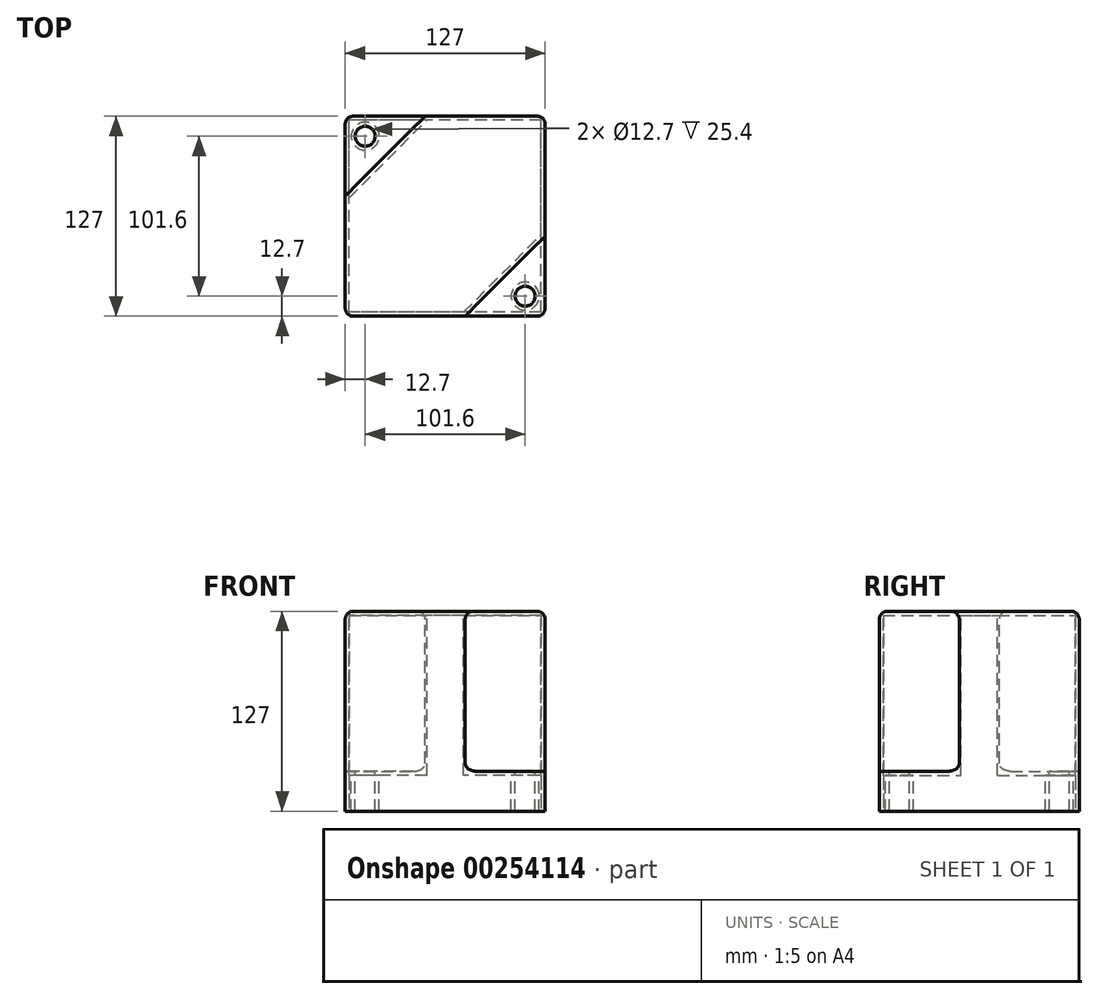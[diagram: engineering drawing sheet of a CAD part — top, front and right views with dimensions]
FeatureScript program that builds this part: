
annotation { "Feature Type Name" : "Feature", "Feature Type Description" : "" }
export const myFeature = defineFeature(function(context is Context, id is Id, definition is map)
    precondition{}
    {
        {
            var Q0;
            Q0=qCreatedBy(makeId("Top.planeOp"),FACE);
            var sketch = newSketch(context, id + "F0", { "sketchPlane" : qUnion([Q0])});
            skLineSegment(sketch, "E0.bottom", {"start": v(63.5, -63.5) * mm, "end": v(-63.5, -63.5) * mm});
            skLineSegment(sketch, "E0.top", {"start": v(63.5, 63.5) * mm, "end": v(-63.5, 63.5) * mm});
            skLineSegment(sketch, "E0.left", {"start": v(63.5, -63.5) * mm, "end": v(63.5, 63.5) * mm});
            skLineSegment(sketch, "E0.right", {"start": v(-63.5, -63.5) * mm, "end": v(-63.5, 63.5) * mm});
            skPoint(sketch, "E0.middle", {"position": v(0, 0) * mm});
            skSolve(sketch);
        }
        {
            var Q0;
            Q0=makeQuery(id+"F0.imprint","IMPRINT",FACE,{"disambiguationData":[TD([[makeQuery(id+"F0.imprint","IMPRINT",EDGE,{"derivedFrom":sQuery(id+"F0.wireOp",EDGE,"E0.bottom")}),-1.0]])]});
            extrude(context, id + "F1", {"entities" : qUnion([Q0]), "depth" : 127 * mm});
        }
        {
            var Q0;
            Q0=makeQuery(id+"F1.opExtrude","CAP_FACE",FACE,{"disambiguationData":[OSD([sQuery(id+"F0.wireOp",EDGE,"E0.bottom"),sQuery(id+"F0.wireOp",EDGE,"E0.top"),sQuery(id+"F0.wireOp",EDGE,"E0.left"),sQuery(id+"F0.wireOp",EDGE,"E0.right")])],"isStart":false});
            var sketch = newSketch(context, id + "F2", { "sketchPlane" : qUnion([Q0])});
            skLineSegment(sketch, "E1", {"start": v(-63.5, 63.5) * mm, "end": v(-63.5, 12.7) * mm});
            skLineSegment(sketch, "E2", {"start": v(-63.5, 63.5) * mm, "end": v(-12.7, 63.5) * mm});
            skLineSegment(sketch, "E3", {"start": v(63.5, -63.5) * mm, "end": v(12.7, -63.5) * mm});
            skLineSegment(sketch, "E4", {"start": v(63.5, -63.5) * mm, "end": v(63.5, -12.7) * mm});
            skLineSegment(sketch, "E5", {"start": v(-63.5, 12.7) * mm, "end": v(-12.7, 63.5) * mm});
            skLineSegment(sketch, "E6", {"start": v(12.7, -63.5) * mm, "end": v(63.5, -12.7) * mm});
            skSolve(sketch);
        }
        {
            var Q0;
            Q0 = qSketchRegion(id + "F2", true);
            extrude(context, id + "F3", {"entities" : qUnion([Q0]), "operationType" : NewBodyOperationType.REMOVE, "oppositeDirection" : true, "depth" : 101.6 * mm});
        }
        {
            var Q0;
            Q0=makeQuery(id+"F3.boolean.opBoolean","COPY",FACE,{"derivedFrom":makeQuery(id+"F3.opExtrude","CAP_FACE",FACE,{"disambiguationData":[OSD([sQuery(id+"F2.wireOp",EDGE,"E1"),sQuery(id+"F2.wireOp",EDGE,"E2"),sQuery(id+"F2.wireOp",EDGE,"E5")])],"isStart":false})});
            var sketch = newSketch(context, id + "F4", { "sketchPlane" : qUnion([Q0])});
            skCircle(sketch, "E7", {"center": v(-50.8, 50.8) * mm, "radius": 6.35 * mm});
            skCircle(sketch, "E8", {"center": v(50.8, -50.8) * mm, "radius": 6.35 * mm});
            skSolve(sketch);
        }
        {
            var Q0;
            Q0=makeQuery(id+"F4.imprint","IMPRINT",FACE,{"disambiguationData":[TD([[makeQuery(id+"F4.imprint","IMPRINT",EDGE,{"derivedFrom":sQuery(id+"F4.wireOp",EDGE,"E7")}),1.0]])]});
            var Q1;
            Q1=makeQuery(id+"F4.imprint","IMPRINT",FACE,{"disambiguationData":[TD([[makeQuery(id+"F4.imprint","IMPRINT",EDGE,{"derivedFrom":sQuery(id+"F4.wireOp",EDGE,"E8")}),1.0]])]});
            extrude(context, id + "F5", {"entities" : qUnion([Q0, Q1]), "operationType" : NewBodyOperationType.REMOVE, "oppositeDirection" : true, "depth" : 203.2 * mm});
        }
        {
            var Q0;
            Q0=makeQuery(id+"F1.opExtrude","CAP_FACE",FACE,{"disambiguationData":[OSD([sQuery(id+"F0.wireOp",EDGE,"E0.bottom"),sQuery(id+"F0.wireOp",EDGE,"E0.top"),sQuery(id+"F0.wireOp",EDGE,"E0.left"),sQuery(id+"F0.wireOp",EDGE,"E0.right")])],"isStart":true});
            shell(context, id + "F6", {"entities" : qUnion([Q0]), "thickness" : 2.54 * mm});
        }
        {
            var Q0;
            Q0=makeQuery(id+"F3.boolean.opBoolean","COPY",EDGE,{"derivedFrom":makeQuery(id+"F3.opExtrude","CAP_EDGE",EDGE,{"disambiguationData":[OSD([sQuery(id+"F2.wireOp",EDGE,"E6")])],"isStart":true})});
            var Q1;
            Q1=makeQuery(id+"F1.opExtrude","CAP_EDGE",EDGE,{"disambiguationData":[OSD([sQuery(id+"F0.wireOp",EDGE,"E0.bottom")])],"isStart":false});
            var Q2;
            Q2=makeQuery(id+"F3.boolean.opBoolean","COPY",EDGE,{"derivedFrom":makeQuery(id+"F3.opExtrude","SWEPT_EDGE",EDGE,{"disambiguationData":[OSD([sQuery(id+"F0.wireOp",EDGE,"E0.bottom"),sQuery(id+"F2.wireOp",EDGE,"E3"),sQuery(id+"F2.wireOp",EDGE,"E6")])]})});
            var Q3;
            Q3=makeQuery(id+"F3.boolean.opBoolean","COPY",EDGE,{"derivedFrom":makeQuery(id+"F3.opExtrude","SWEPT_EDGE",EDGE,{"disambiguationData":[OSD([sQuery(id+"F0.wireOp",EDGE,"E0.left"),sQuery(id+"F2.wireOp",EDGE,"E4"),sQuery(id+"F2.wireOp",EDGE,"E6")])]})});
            var Q4;
            Q4=makeQuery(id+"F1.opExtrude","CAP_EDGE",EDGE,{"disambiguationData":[OSD([sQuery(id+"F0.wireOp",EDGE,"E0.left")])],"isStart":false});
            var Q5;
            Q5=makeQuery(id+"F3.boolean.opBoolean","COPY",EDGE,{"derivedFrom":makeQuery(id+"F3.opExtrude","CAP_EDGE",EDGE,{"disambiguationData":[OSD([sQuery(id+"F2.wireOp",EDGE,"E4")])],"isStart":false})});
            var Q6;
            Q6=makeQuery(id+"F3.boolean.opBoolean","COPY",EDGE,{"derivedFrom":makeQuery(id+"F3.opExtrude","CAP_EDGE",EDGE,{"disambiguationData":[OSD([sQuery(id+"F2.wireOp",EDGE,"E3")])],"isStart":false})});
            var Q7;
            Q7=makeQuery(id+"F3.boolean.opBoolean","COPY",EDGE,{"derivedFrom":makeQuery(id+"F3.opExtrude","CAP_EDGE",EDGE,{"disambiguationData":[OSD([sQuery(id+"F2.wireOp",EDGE,"E6")])],"isStart":false})});
            var Q8;
            Q8=makeQuery(id+"F1.opExtrude","SWEPT_EDGE",EDGE,{"disambiguationData":[OSD([sQuery(id+"F0.wireOp",EDGE,"E0.bottom"),sQuery(id+"F0.wireOp",EDGE,"E0.left")])]});
            var Q9;
            Q9=makeQuery(id+"F1.opExtrude","CAP_EDGE",EDGE,{"disambiguationData":[OSD([sQuery(id+"F0.wireOp",EDGE,"E0.top")])],"isStart":false});
            var Q10;
            Q10=makeQuery(id+"F3.boolean.opBoolean","COPY",EDGE,{"derivedFrom":makeQuery(id+"F3.opExtrude","CAP_EDGE",EDGE,{"disambiguationData":[OSD([sQuery(id+"F2.wireOp",EDGE,"E5")])],"isStart":true})});
            var Q11;
            Q11=makeQuery(id+"F1.opExtrude","CAP_EDGE",EDGE,{"disambiguationData":[OSD([sQuery(id+"F0.wireOp",EDGE,"E0.right")])],"isStart":false});
            var Q12;
            Q12=makeQuery(id+"F3.boolean.opBoolean","COPY",EDGE,{"derivedFrom":makeQuery(id+"F3.opExtrude","SWEPT_EDGE",EDGE,{"disambiguationData":[OSD([sQuery(id+"F0.wireOp",EDGE,"E0.top"),sQuery(id+"F2.wireOp",EDGE,"E2"),sQuery(id+"F2.wireOp",EDGE,"E5")])]})});
            var Q13;
            Q13=makeQuery(id+"F3.boolean.opBoolean","COPY",EDGE,{"derivedFrom":makeQuery(id+"F3.opExtrude","SWEPT_EDGE",EDGE,{"disambiguationData":[OSD([sQuery(id+"F0.wireOp",EDGE,"E0.right"),sQuery(id+"F2.wireOp",EDGE,"E1"),sQuery(id+"F2.wireOp",EDGE,"E5")])]})});
            var Q14;
            Q14=makeQuery(id+"F3.boolean.opBoolean","COPY",EDGE,{"derivedFrom":makeQuery(id+"F3.opExtrude","CAP_EDGE",EDGE,{"disambiguationData":[OSD([sQuery(id+"F2.wireOp",EDGE,"E5")])],"isStart":false})});
            var Q15;
            Q15=makeQuery(id+"F1.opExtrude","SWEPT_EDGE",EDGE,{"disambiguationData":[OSD([sQuery(id+"F0.wireOp",EDGE,"E0.top"),sQuery(id+"F0.wireOp",EDGE,"E0.left")])]});
            var Q16;
            Q16=makeQuery(id+"F1.opExtrude","SWEPT_EDGE",EDGE,{"disambiguationData":[OSD([sQuery(id+"F0.wireOp",EDGE,"E0.bottom"),sQuery(id+"F0.wireOp",EDGE,"E0.right")])]});
            var Q17;
            Q17=makeQuery(id+"F1.opExtrude","SWEPT_EDGE",EDGE,{"disambiguationData":[OSD([sQuery(id+"F0.wireOp",EDGE,"E0.top"),sQuery(id+"F0.wireOp",EDGE,"E0.right")])]});
            fillet(context, id + "F7", {"entities" : qUnion([Q0, Q1, Q2, Q3, Q4, Q5, Q6, Q7, Q8, Q9, Q10, Q11, Q12, Q13, Q14, Q15, Q16, Q17]), "radius" : 5.08 * mm, "tangentPropagation" : true, "allowEdgeOverflow" : false});
        }
    });
